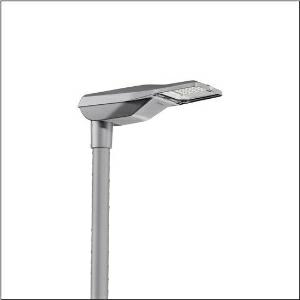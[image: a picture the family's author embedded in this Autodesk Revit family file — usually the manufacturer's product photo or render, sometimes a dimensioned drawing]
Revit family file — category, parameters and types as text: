
# Revit family: streetlight_sl_21_iq_micro___st0_8a_5xe1c41d08db_9d18
name_source: partatom
category: Lighting Fixtures
units: mm (PartAtom-declared; Revit-internal decimal feet)

## family parameters
Cut with Voids When Loaded = No
Host = Face
Light Source = No
Part Type = Normal
Room Calculation Point = No
Round Connector Dimension = Use Diameter
Shared = No

## types (1)
- --- (1 x LED, 5010 lm, 36.4 W, 4000K)
    Apparent Load = 36 VA
    CIE Flux Codes = 38 75 97 100 100
    Color Rendering = 70
    Color Temperature = 4000K
    Default Elevation = 1800 mm
    Description = Streetlight SL 21 iQ micro, mast luminaire, primary light control with lens, of PMMA, primary optical cover: cover, of toughened safety glass, transparent, light distribution: ST0.8a, light emission: direct distribution, primary light characteristic: asymmetric, installation type: post-top, side-entry, LED, High Power LED, rated luminous flux: 5.010lm, luminous efficacy: 138lm/W, light colour: 740, colour temperature: 4000K, control gear: iQ-Comfort, control: Auto-Match, Temp-Guard, Lumen-Switch, Night-Set, Smart-Wire, Light-Fading, Desk-Remote (wireless, voltage-free reading and setting of iQ features in the workshop via application-optimized NFC function/RFID function), optimised constant luminous flux control (CLO 2.0), pre-setting: linear dimming characteristic, mains connection: 220..240V, AC, 50/60Hz, start of lifetime: 36W, end of service life: 38W, reduction: 16W, luminaire housing, of diecast aluminium, powder-coated, SITECO metallic grey (DB 702S), corrosivity category C5 high according to DIN EN ISO 12944, please order mast flange separately, inclination adjustable: 0°, 5°, 10°, 15°, sealing non-destructively replaceable, multi-level sealing system, length: 528mm, width: 235mm, height: 110mm, mast flange for spigot size: 42mm (side-entry): 5XC10008XM4, 60/48mm (side-entry/post-top): 5XC10108XM2, 76/60mm (side-entry/post-top): 5XC10108XM1, protection rating (complete): IP66, insulation class (complete): insulation class II (safety insulation), certification: CE, ENEC, ENEC+, VDE, impact resistance: IK10, permissible operating ambient temperature for outdoor applications: -40..+50°C, standard-compliant lighting for roads and squares, packaging unit: 1 piece

Light Distribution: ST0.8a
    Height = 110 mm
    Lamp = 1 x LED
    Lamp Light Flux = 5010 lm
    Lamp Power = 36.4 W
    Lamp count = 1
    Length = 528 mm
    Luminous efficacy = 138 lm/W
    Manufacturer = Siteco
    ModVariant = No
    Model = 5XE1C41D08DB
    Number of Poles = 1
    OnlyDefault = Yes
    Power Factor = 1
    Product Name = Streetlight SL 21 iQ micro | ST0.8a
    Product group = mast luminaire | pylon top
    ProductGroupID = 6100
    Protection Class = Protection class II
    Protection Degree = IP 66
    RLX_Detail_Level = 1
    RLX_Emergency_Light_Flux = 0 lm
    RLX_Emergency_Type = 0
    RLX_Emergency_Type_DB = No
    RlxData = <blob elided: 99313 chars, md5=14933c73>
    Socket = socket
    Standby Power = 0 W
    System Light Flux = 5010 lm
    System Power = 36 W
    Type Comments = factory setting: luminous flux: 100 % | dim-lin: 254 | 715 mA
    Type Image = l_1006881.jpg
    URL = http://relux.com
    VarID = @adj_153995
    Voltage = 0 V
    Weight = 0.00 kg
    Width = 235 mm

## geometry (parser evidence)
native form markers: Blend x4, Sweep x9
no freeform markers — native parametric forms only
